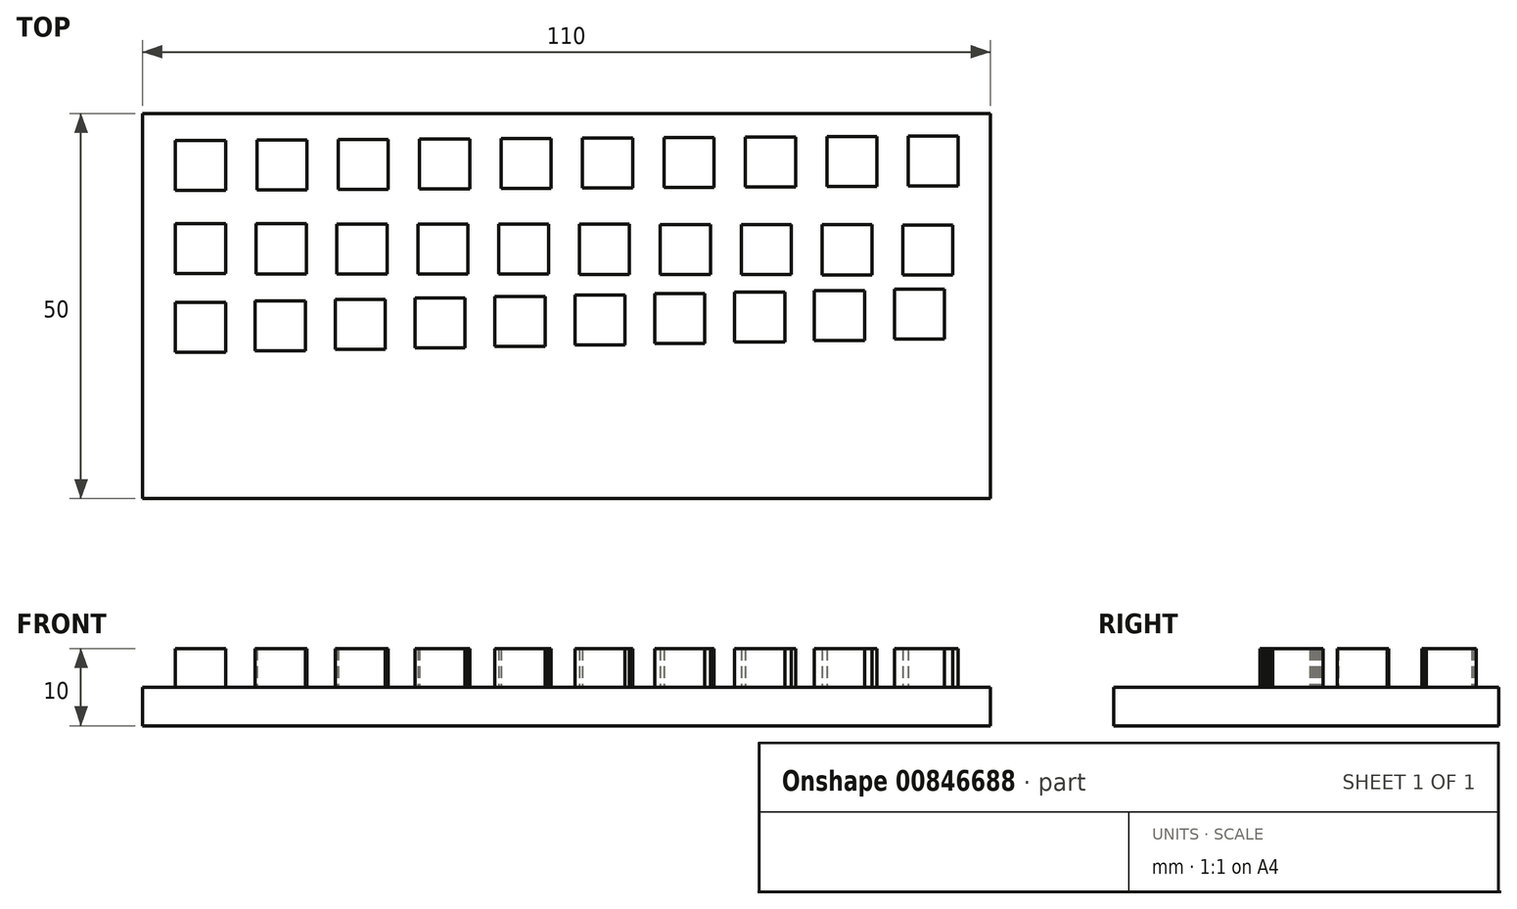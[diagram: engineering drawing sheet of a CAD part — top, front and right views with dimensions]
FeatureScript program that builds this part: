
annotation { "Feature Type Name" : "Feature", "Feature Type Description" : "" }
export const myFeature = defineFeature(function(context is Context, id is Id, definition is map)
    precondition{}
    {
        {
            var Q0;
            Q0=qCreatedBy(makeId("Top.planeOp"),FACE);
            var sketch = newSketch(context, id + "F0", { "sketchPlane" : qUnion([Q0])});
            skLineSegment(sketch, "E0.bottom", {"start": v(-52.41, 30.53) * mm, "end": v(57.59, 30.53) * mm});
            skLineSegment(sketch, "E0.top", {"start": v(-52.41, -19.47) * mm, "end": v(57.59, -19.47) * mm});
            skLineSegment(sketch, "E0.left", {"start": v(-52.41, 30.53) * mm, "end": v(-52.41, -19.47) * mm});
            skLineSegment(sketch, "E0.right", {"start": v(57.59, 30.53) * mm, "end": v(57.59, -19.47) * mm});
            skSolve(sketch);
        }
        {
            var Q0;
            Q0 = qSketchRegion(id + "F0", true);
            extrude(context, id + "F1", {"entities" : qUnion([Q0]), "depth" : 5 * mm, "offsetDistance" : 25 * mm});
        }
        {
            var Q0;
            Q0=makeQuery(id+"F1.opExtrude","CAP_FACE",FACE,{"disambiguationData":[OSD([sQuery(id+"F0.wireOp",EDGE,"E0.bottom"),sQuery(id+"F0.wireOp",EDGE,"E0.top"),sQuery(id+"F0.wireOp",EDGE,"E0.left"),sQuery(id+"F0.wireOp",EDGE,"E0.right")])],"isStart":false});
            var sketch = newSketch(context, id + "F2", { "sketchPlane" : qUnion([Q0])});
            skLineSegment(sketch, "E1.bottom", {"start": v(-48.17, 27.04) * mm, "end": v(-41.67, 27.04) * mm});
            skLineSegment(sketch, "E1.top", {"start": v(-48.17, 20.54) * mm, "end": v(-41.67, 20.54) * mm});
            skLineSegment(sketch, "E1.left", {"start": v(-48.17, 27.04) * mm, "end": v(-48.17, 20.54) * mm});
            skLineSegment(sketch, "E1.right", {"start": v(-41.67, 27.04) * mm, "end": v(-41.67, 20.54) * mm});
            skPoint(sketch, "E1.middle", {"position": v(-44.92, 23.79) * mm});
            skLineSegment(sketch, "E2.1.0.0", {"start": v(-37.6, 27.1) * mm, "end": v(-31.1, 27.1) * mm});
            skLineSegment(sketch, "E2.1.0.1", {"start": v(-31.1, 27.1) * mm, "end": v(-31.1, 20.6) * mm});
            skLineSegment(sketch, "E2.1.0.2", {"start": v(-37.6, 20.6) * mm, "end": v(-31.1, 20.6) * mm});
            skLineSegment(sketch, "E2.1.0.3", {"start": v(-37.6, 27.1) * mm, "end": v(-37.6, 20.6) * mm});
            skLineSegment(sketch, "E2.2.0.0", {"start": v(-27.03, 27.16) * mm, "end": v(-20.53, 27.16) * mm});
            skLineSegment(sketch, "E2.2.0.1", {"start": v(-20.53, 27.16) * mm, "end": v(-20.53, 20.66) * mm});
            skLineSegment(sketch, "E2.2.0.2", {"start": v(-27.03, 20.66) * mm, "end": v(-20.53, 20.66) * mm});
            skLineSegment(sketch, "E2.2.0.3", {"start": v(-27.03, 27.16) * mm, "end": v(-27.03, 20.66) * mm});
            skLineSegment(sketch, "E2.3.0.0", {"start": v(-16.46, 27.23) * mm, "end": v(-9.96, 27.23) * mm});
            skLineSegment(sketch, "E2.3.0.1", {"start": v(-9.96, 27.23) * mm, "end": v(-9.96, 20.73) * mm});
            skLineSegment(sketch, "E2.3.0.2", {"start": v(-16.46, 20.73) * mm, "end": v(-9.96, 20.73) * mm});
            skLineSegment(sketch, "E2.3.0.3", {"start": v(-16.46, 27.23) * mm, "end": v(-16.46, 20.73) * mm});
            skLineSegment(sketch, "E2.4.0.0", {"start": v(-5.9, 27.3) * mm, "end": v(0.6, 27.3) * mm});
            skLineSegment(sketch, "E2.4.0.1", {"start": v(0.6, 27.3) * mm, "end": v(0.6, 20.8) * mm});
            skLineSegment(sketch, "E2.4.0.2", {"start": v(-5.9, 20.8) * mm, "end": v(0.6, 20.8) * mm});
            skLineSegment(sketch, "E2.4.0.3", {"start": v(-5.9, 27.3) * mm, "end": v(-5.9, 20.8) * mm});
            skLineSegment(sketch, "E2.5.0.0", {"start": v(4.68, 27.36) * mm, "end": v(11.18, 27.36) * mm});
            skLineSegment(sketch, "E2.5.0.1", {"start": v(11.18, 27.36) * mm, "end": v(11.18, 20.86) * mm});
            skLineSegment(sketch, "E2.5.0.2", {"start": v(4.68, 20.86) * mm, "end": v(11.18, 20.86) * mm});
            skLineSegment(sketch, "E2.5.0.3", {"start": v(4.68, 27.36) * mm, "end": v(4.68, 20.86) * mm});
            skLineSegment(sketch, "E2.6.0.0", {"start": v(15.25, 27.42) * mm, "end": v(21.75, 27.42) * mm});
            skLineSegment(sketch, "E2.6.0.1", {"start": v(21.75, 27.42) * mm, "end": v(21.75, 20.92) * mm});
            skLineSegment(sketch, "E2.6.0.2", {"start": v(15.25, 20.92) * mm, "end": v(21.75, 20.92) * mm});
            skLineSegment(sketch, "E2.6.0.3", {"start": v(15.25, 27.42) * mm, "end": v(15.25, 20.92) * mm});
            skLineSegment(sketch, "E2.7.0.0", {"start": v(25.81, 27.48) * mm, "end": v(32.31, 27.48) * mm});
            skLineSegment(sketch, "E2.7.0.1", {"start": v(32.31, 27.48) * mm, "end": v(32.31, 20.98) * mm});
            skLineSegment(sketch, "E2.7.0.2", {"start": v(25.81, 20.98) * mm, "end": v(32.31, 20.98) * mm});
            skLineSegment(sketch, "E2.7.0.3", {"start": v(25.81, 27.48) * mm, "end": v(25.81, 20.98) * mm});
            skLineSegment(sketch, "E2.8.0.0", {"start": v(36.38, 27.55) * mm, "end": v(42.88, 27.55) * mm});
            skLineSegment(sketch, "E2.8.0.1", {"start": v(42.88, 27.55) * mm, "end": v(42.88, 21.05) * mm});
            skLineSegment(sketch, "E2.8.0.2", {"start": v(36.38, 21.05) * mm, "end": v(42.88, 21.05) * mm});
            skLineSegment(sketch, "E2.8.0.3", {"start": v(36.38, 27.55) * mm, "end": v(36.38, 21.05) * mm});
            skLineSegment(sketch, "E2.9.0.0", {"start": v(46.95, 27.61) * mm, "end": v(53.45, 27.61) * mm});
            skLineSegment(sketch, "E2.9.0.1", {"start": v(53.45, 27.61) * mm, "end": v(53.45, 21.11) * mm});
            skLineSegment(sketch, "E2.9.0.2", {"start": v(46.95, 21.11) * mm, "end": v(53.45, 21.11) * mm});
            skLineSegment(sketch, "E2.9.0.3", {"start": v(46.95, 27.61) * mm, "end": v(46.95, 21.11) * mm});
            skLineSegment(sketch, "E2.direction1", {"start": v(-48.17, 27.04) * mm, "end": v(-37.6, 27.1) * mm, "construction": true});
            skLineSegment(sketch, "E3.bottom", {"start": v(-48.17, 16.22) * mm, "end": v(-41.67, 16.22) * mm});
            skLineSegment(sketch, "E3.top", {"start": v(-48.17, 9.72) * mm, "end": v(-41.67, 9.72) * mm});
            skLineSegment(sketch, "E3.left", {"start": v(-48.17, 16.22) * mm, "end": v(-48.17, 9.72) * mm});
            skLineSegment(sketch, "E3.right", {"start": v(-41.67, 16.22) * mm, "end": v(-41.67, 9.72) * mm});
            skPoint(sketch, "E3.middle", {"position": v(-44.92, 12.97) * mm});
            skLineSegment(sketch, "E4.1.0.0", {"start": v(-37.68, 16.2) * mm, "end": v(-31.18, 16.2) * mm});
            skLineSegment(sketch, "E4.1.0.1", {"start": v(-37.68, 16.2) * mm, "end": v(-37.68, 9.7) * mm});
            skLineSegment(sketch, "E4.1.0.2", {"start": v(-31.18, 16.2) * mm, "end": v(-31.18, 9.7) * mm});
            skLineSegment(sketch, "E4.1.0.3", {"start": v(-37.68, 9.7) * mm, "end": v(-31.18, 9.7) * mm});
            skLineSegment(sketch, "E4.2.0.0", {"start": v(-27.19, 16.18) * mm, "end": v(-20.69, 16.18) * mm});
            skLineSegment(sketch, "E4.2.0.1", {"start": v(-27.19, 16.18) * mm, "end": v(-27.19, 9.68) * mm});
            skLineSegment(sketch, "E4.2.0.2", {"start": v(-20.69, 16.18) * mm, "end": v(-20.69, 9.68) * mm});
            skLineSegment(sketch, "E4.2.0.3", {"start": v(-27.19, 9.68) * mm, "end": v(-20.69, 9.68) * mm});
            skLineSegment(sketch, "E4.3.0.0", {"start": v(-16.7, 16.16) * mm, "end": v(-10.2, 16.16) * mm});
            skLineSegment(sketch, "E4.3.0.1", {"start": v(-16.7, 16.16) * mm, "end": v(-16.7, 9.66) * mm});
            skLineSegment(sketch, "E4.3.0.2", {"start": v(-10.2, 16.16) * mm, "end": v(-10.2, 9.66) * mm});
            skLineSegment(sketch, "E4.3.0.3", {"start": v(-16.7, 9.66) * mm, "end": v(-10.2, 9.66) * mm});
            skLineSegment(sketch, "E4.4.0.0", {"start": v(-6.2, 16.15) * mm, "end": v(0.3, 16.15) * mm});
            skLineSegment(sketch, "E4.4.0.1", {"start": v(-6.2, 16.15) * mm, "end": v(-6.2, 9.65) * mm});
            skLineSegment(sketch, "E4.4.0.2", {"start": v(0.3, 16.15) * mm, "end": v(0.3, 9.65) * mm});
            skLineSegment(sketch, "E4.4.0.3", {"start": v(-6.2, 9.65) * mm, "end": v(0.3, 9.65) * mm});
            skLineSegment(sketch, "E4.5.0.0", {"start": v(4.28, 16.13) * mm, "end": v(10.78, 16.13) * mm});
            skLineSegment(sketch, "E4.5.0.1", {"start": v(4.28, 16.13) * mm, "end": v(4.28, 9.63) * mm});
            skLineSegment(sketch, "E4.5.0.2", {"start": v(10.78, 16.13) * mm, "end": v(10.78, 9.63) * mm});
            skLineSegment(sketch, "E4.5.0.3", {"start": v(4.28, 9.63) * mm, "end": v(10.78, 9.63) * mm});
            skLineSegment(sketch, "E4.6.0.0", {"start": v(14.77, 16.1) * mm, "end": v(21.27, 16.1) * mm});
            skLineSegment(sketch, "E4.6.0.1", {"start": v(14.77, 16.1) * mm, "end": v(14.77, 9.6) * mm});
            skLineSegment(sketch, "E4.6.0.2", {"start": v(21.27, 16.1) * mm, "end": v(21.27, 9.6) * mm});
            skLineSegment(sketch, "E4.6.0.3", {"start": v(14.77, 9.6) * mm, "end": v(21.27, 9.6) * mm});
            skLineSegment(sketch, "E4.7.0.0", {"start": v(25.26, 16.1) * mm, "end": v(31.76, 16.1) * mm});
            skLineSegment(sketch, "E4.7.0.1", {"start": v(25.26, 16.1) * mm, "end": v(25.26, 9.6) * mm});
            skLineSegment(sketch, "E4.7.0.2", {"start": v(31.76, 16.1) * mm, "end": v(31.76, 9.6) * mm});
            skLineSegment(sketch, "E4.7.0.3", {"start": v(25.26, 9.6) * mm, "end": v(31.76, 9.6) * mm});
            skLineSegment(sketch, "E4.8.0.0", {"start": v(35.75, 16.07) * mm, "end": v(42.25, 16.07) * mm});
            skLineSegment(sketch, "E4.8.0.1", {"start": v(35.75, 16.07) * mm, "end": v(35.75, 9.57) * mm});
            skLineSegment(sketch, "E4.8.0.2", {"start": v(42.25, 16.07) * mm, "end": v(42.25, 9.57) * mm});
            skLineSegment(sketch, "E4.8.0.3", {"start": v(35.75, 9.57) * mm, "end": v(42.25, 9.57) * mm});
            skLineSegment(sketch, "E4.9.0.0", {"start": v(46.24, 16.05) * mm, "end": v(52.74, 16.05) * mm});
            skLineSegment(sketch, "E4.9.0.1", {"start": v(46.24, 16.05) * mm, "end": v(46.24, 9.55) * mm});
            skLineSegment(sketch, "E4.9.0.2", {"start": v(52.74, 16.05) * mm, "end": v(52.74, 9.55) * mm});
            skLineSegment(sketch, "E4.9.0.3", {"start": v(46.24, 9.55) * mm, "end": v(52.74, 9.55) * mm});
            skLineSegment(sketch, "E4.direction1", {"start": v(-48.17, 16.22) * mm, "end": v(-37.68, 16.2) * mm, "construction": true});
            skLineSegment(sketch, "E5.bottom", {"start": v(-48.17, 6.01) * mm, "end": v(-41.67, 6.01) * mm});
            skLineSegment(sketch, "E5.top", {"start": v(-48.17, -0.49) * mm, "end": v(-41.67, -0.49) * mm});
            skLineSegment(sketch, "E5.left", {"start": v(-48.17, 6.01) * mm, "end": v(-48.17, -0.49) * mm});
            skLineSegment(sketch, "E5.right", {"start": v(-41.67, 6.01) * mm, "end": v(-41.67, -0.49) * mm});
            skPoint(sketch, "E5.middle", {"position": v(-44.92, 2.76) * mm});
            skLineSegment(sketch, "E6.1.0.0", {"start": v(-37.8, 6.2) * mm, "end": v(-37.8, -0.3) * mm});
            skLineSegment(sketch, "E6.1.0.1", {"start": v(-31.3, 6.2) * mm, "end": v(-31.3, -0.3) * mm});
            skLineSegment(sketch, "E6.1.0.2", {"start": v(-37.8, 6.2) * mm, "end": v(-31.3, 6.2) * mm});
            skLineSegment(sketch, "E6.1.0.3", {"start": v(-37.8, -0.3) * mm, "end": v(-31.3, -0.3) * mm});
            skLineSegment(sketch, "E6.2.0.0", {"start": v(-27.43, 6.39) * mm, "end": v(-27.43, -0.11) * mm});
            skLineSegment(sketch, "E6.2.0.1", {"start": v(-20.93, 6.39) * mm, "end": v(-20.93, -0.11) * mm});
            skLineSegment(sketch, "E6.2.0.2", {"start": v(-27.43, 6.39) * mm, "end": v(-20.93, 6.39) * mm});
            skLineSegment(sketch, "E6.2.0.3", {"start": v(-27.43, -0.11) * mm, "end": v(-20.93, -0.11) * mm});
            skLineSegment(sketch, "E6.3.0.0", {"start": v(-17.06, 6.58) * mm, "end": v(-17.06, 0.08) * mm});
            skLineSegment(sketch, "E6.3.0.1", {"start": v(-10.56, 6.58) * mm, "end": v(-10.56, 0.08) * mm});
            skLineSegment(sketch, "E6.3.0.2", {"start": v(-17.06, 6.58) * mm, "end": v(-10.56, 6.58) * mm});
            skLineSegment(sketch, "E6.3.0.3", {"start": v(-17.06, 0.08) * mm, "end": v(-10.56, 0.08) * mm});
            skLineSegment(sketch, "E6.4.0.0", {"start": v(-6.7, 6.77) * mm, "end": v(-6.7, 0.27) * mm});
            skLineSegment(sketch, "E6.4.0.1", {"start": v(-0.2, 6.77) * mm, "end": v(-0.2, 0.27) * mm});
            skLineSegment(sketch, "E6.4.0.2", {"start": v(-6.7, 6.77) * mm, "end": v(-0.2, 6.77) * mm});
            skLineSegment(sketch, "E6.4.0.3", {"start": v(-6.7, 0.27) * mm, "end": v(-0.2, 0.27) * mm});
            skLineSegment(sketch, "E6.5.0.0", {"start": v(3.68, 6.96) * mm, "end": v(3.68, 0.46) * mm});
            skLineSegment(sketch, "E6.5.0.1", {"start": v(10.18, 6.96) * mm, "end": v(10.18, 0.46) * mm});
            skLineSegment(sketch, "E6.5.0.2", {"start": v(3.68, 6.96) * mm, "end": v(10.18, 6.96) * mm});
            skLineSegment(sketch, "E6.5.0.3", {"start": v(3.68, 0.46) * mm, "end": v(10.18, 0.46) * mm});
            skLineSegment(sketch, "E6.6.0.0", {"start": v(14.04, 7.15) * mm, "end": v(14.04, 0.65) * mm});
            skLineSegment(sketch, "E6.6.0.1", {"start": v(20.54, 7.15) * mm, "end": v(20.54, 0.65) * mm});
            skLineSegment(sketch, "E6.6.0.2", {"start": v(14.04, 7.15) * mm, "end": v(20.54, 7.15) * mm});
            skLineSegment(sketch, "E6.6.0.3", {"start": v(14.04, 0.65) * mm, "end": v(20.54, 0.65) * mm});
            skLineSegment(sketch, "E6.7.0.0", {"start": v(24.41, 7.33) * mm, "end": v(24.41, 0.83) * mm});
            skLineSegment(sketch, "E6.7.0.1", {"start": v(30.91, 7.33) * mm, "end": v(30.91, 0.83) * mm});
            skLineSegment(sketch, "E6.7.0.2", {"start": v(24.41, 7.33) * mm, "end": v(30.91, 7.33) * mm});
            skLineSegment(sketch, "E6.7.0.3", {"start": v(24.41, 0.83) * mm, "end": v(30.91, 0.83) * mm});
            skLineSegment(sketch, "E6.8.0.0", {"start": v(34.78, 7.52) * mm, "end": v(34.78, 1.02) * mm});
            skLineSegment(sketch, "E6.8.0.1", {"start": v(41.28, 7.52) * mm, "end": v(41.28, 1.02) * mm});
            skLineSegment(sketch, "E6.8.0.2", {"start": v(34.78, 7.52) * mm, "end": v(41.28, 7.52) * mm});
            skLineSegment(sketch, "E6.8.0.3", {"start": v(34.78, 1.02) * mm, "end": v(41.28, 1.02) * mm});
            skLineSegment(sketch, "E6.9.0.0", {"start": v(45.15, 7.71) * mm, "end": v(45.15, 1.21) * mm});
            skLineSegment(sketch, "E6.9.0.1", {"start": v(51.65, 7.71) * mm, "end": v(51.65, 1.21) * mm});
            skLineSegment(sketch, "E6.9.0.2", {"start": v(45.15, 7.71) * mm, "end": v(51.65, 7.71) * mm});
            skLineSegment(sketch, "E6.9.0.3", {"start": v(45.15, 1.21) * mm, "end": v(51.65, 1.21) * mm});
            skLineSegment(sketch, "E6.direction1", {"start": v(-48.17, -0.49) * mm, "end": v(-37.8, -0.3) * mm, "construction": true});
            skSolve(sketch);
        }
        {
            var Q0;
            Q0 = qSketchRegion(id + "F2", true);
            extrude(context, id + "F3", {"entities" : qUnion([Q0]), "operationType" : NewBodyOperationType.ADD, "depth" : 5 * mm, "offsetDistance" : 25 * mm});
        }
    });
